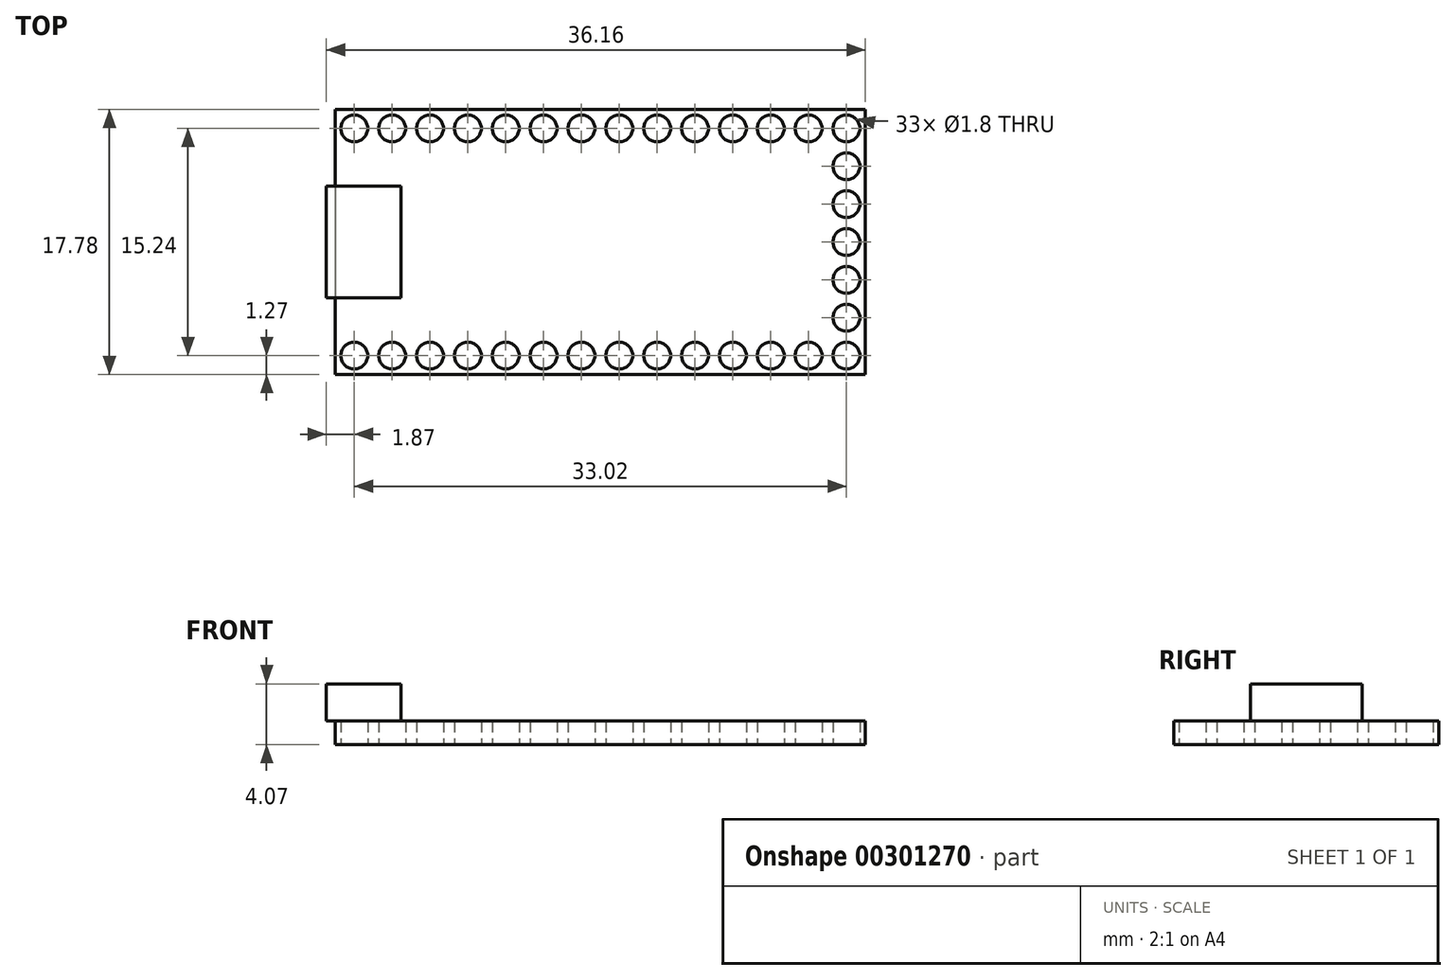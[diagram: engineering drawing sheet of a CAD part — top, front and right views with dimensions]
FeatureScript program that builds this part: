
annotation { "Feature Type Name" : "Feature", "Feature Type Description" : "" }
export const myFeature = defineFeature(function(context is Context, id is Id, definition is map)
    precondition{}
    {
        {
            var Q0;
            Q0=qCreatedBy(makeId("Top.planeOp"),FACE);
            var sketch = newSketch(context, id + "F0", { "sketchPlane" : qUnion([Q0])});
            skLineSegment(sketch, "E0.bottom", {"start": v(0, 8.9) * mm, "end": v(35.56, 8.9) * mm});
            skLineSegment(sketch, "E0.top", {"start": v(0, -8.9) * mm, "end": v(35.56, -8.89) * mm});
            skLineSegment(sketch, "E0.left", {"start": v(0, 8.9) * mm, "end": v(0, -8.9) * mm});
            skLineSegment(sketch, "E0.right", {"start": v(35.56, 8.9) * mm, "end": v(35.56, -8.89) * mm});
            skLineSegment(sketch, "E1.bottom", {"start": v(4.4, 3.75) * mm, "end": v(-0.6, 3.75) * mm});
            skLineSegment(sketch, "E1.top", {"start": v(4.4, -3.75) * mm, "end": v(-0.6, -3.75) * mm});
            skLineSegment(sketch, "E1.left", {"start": v(4.4, 3.75) * mm, "end": v(4.4, -3.75) * mm});
            skLineSegment(sketch, "E1.right", {"start": v(-0.6, 3.75) * mm, "end": v(-0.6, -3.75) * mm});
            skPoint(sketch, "E2", {"position": v(-0.6, 0) * mm});
            skPoint(sketch, "E3", {"position": v(0, 0) * mm});
            skLineSegment(sketch, "E4", {"start": v(1.27, 7.62) * mm, "end": v(35.56, 7.62) * mm, "construction": true});
            skCircle(sketch, "E5", {"center": v(1.27, 7.62) * mm, "radius": 0.9 * mm});
            skCircle(sketch, "E6.1.0.0", {"center": v(3.8, 7.62) * mm, "radius": 0.9 * mm});
            skCircle(sketch, "E6.2.0.0", {"center": v(6.35, 7.62) * mm, "radius": 0.9 * mm});
            skCircle(sketch, "E6.3.0.0", {"center": v(8.89, 7.62) * mm, "radius": 0.9 * mm});
            skCircle(sketch, "E6.4.0.0", {"center": v(11.43, 7.62) * mm, "radius": 0.9 * mm});
            skCircle(sketch, "E6.5.0.0", {"center": v(13.97, 7.62) * mm, "radius": 0.9 * mm});
            skCircle(sketch, "E6.6.0.0", {"center": v(16.5, 7.62) * mm, "radius": 0.9 * mm});
            skCircle(sketch, "E6.7.0.0", {"center": v(19.05, 7.62) * mm, "radius": 0.9 * mm});
            skCircle(sketch, "E6.8.0.0", {"center": v(21.59, 7.62) * mm, "radius": 0.9 * mm});
            skCircle(sketch, "E6.9.0.0", {"center": v(24.13, 7.62) * mm, "radius": 0.9 * mm});
            skCircle(sketch, "E6.10.0.0", {"center": v(26.67, 7.62) * mm, "radius": 0.9 * mm});
            skCircle(sketch, "E6.11.0.0", {"center": v(29.21, 7.62) * mm, "radius": 0.9 * mm});
            skCircle(sketch, "E6.12.0.0", {"center": v(31.75, 7.62) * mm, "radius": 0.9 * mm});
            skCircle(sketch, "E6.13.0.0", {"center": v(34.29, 7.62) * mm, "radius": 0.9 * mm});
            skLineSegment(sketch, "E6.direction1", {"start": v(1.27, 7.62) * mm, "end": v(3.8, 7.62) * mm, "construction": true});
            skLineSegment(sketch, "E7", {"start": v(0, 0) * mm, "end": v(35.56, 0) * mm, "construction": true});
            skCircle(sketch, "E8.MirrorC", {"center": v(6.35, -7.62) * mm, "radius": 0.9 * mm});
            skCircle(sketch, "E9.MirrorC", {"center": v(24.13, -7.62) * mm, "radius": 0.9 * mm});
            skCircle(sketch, "E10.MirrorC", {"center": v(29.21, -7.62) * mm, "radius": 0.9 * mm});
            skCircle(sketch, "E11.MirrorC", {"center": v(19.05, -7.62) * mm, "radius": 0.9 * mm});
            skCircle(sketch, "E12.MirrorC", {"center": v(8.89, -7.62) * mm, "radius": 0.9 * mm});
            skCircle(sketch, "E13.MirrorC", {"center": v(21.59, -7.62) * mm, "radius": 0.9 * mm});
            skCircle(sketch, "E14.MirrorC", {"center": v(11.43, -7.62) * mm, "radius": 0.9 * mm});
            skCircle(sketch, "E15.MirrorC", {"center": v(3.8, -7.62) * mm, "radius": 0.9 * mm});
            skCircle(sketch, "E16.MirrorC", {"center": v(34.29, -7.62) * mm, "radius": 0.9 * mm});
            skCircle(sketch, "E17.MirrorC", {"center": v(31.75, -7.62) * mm, "radius": 0.9 * mm});
            skCircle(sketch, "E18.MirrorC", {"center": v(13.97, -7.62) * mm, "radius": 0.9 * mm});
            skCircle(sketch, "E19.MirrorC", {"center": v(16.51, -7.62) * mm, "radius": 0.9 * mm});
            skCircle(sketch, "E20.MirrorC", {"center": v(26.67, -7.62) * mm, "radius": 0.9 * mm});
            skCircle(sketch, "E21.MirrorC", {"center": v(1.27, -7.62) * mm, "radius": 0.9 * mm});
            skLineSegment(sketch, "E22.MirrorCS", {"start": v(1.27, -7.62) * mm, "end": v(35.56, -7.62) * mm, "construction": true});
            skLineSegment(sketch, "E23.MirrorCS", {"start": v(1.27, -7.62) * mm, "end": v(3.81, -7.62) * mm, "construction": true});
            skCircle(sketch, "E24.1.0.0", {"center": v(34.3, 5.08) * mm, "radius": 0.9 * mm});
            skCircle(sketch, "E24.2.0.0", {"center": v(34.29, 2.54) * mm, "radius": 0.9 * mm});
            skCircle(sketch, "E24.3.0.0", {"center": v(34.29, 0) * mm, "radius": 0.9 * mm});
            skCircle(sketch, "E24.4.0.0", {"center": v(34.29, -2.54) * mm, "radius": 0.9 * mm});
            skCircle(sketch, "E24.5.0.0", {"center": v(34.29, -5.08) * mm, "radius": 0.9 * mm});
            skLineSegment(sketch, "E24.direction1", {"start": v(34.29, 7.62) * mm, "end": v(34.29, 5.08) * mm, "construction": true});
            skSolve(sketch);
        }
        {
            var Q0;
            {var subQ5=sQuery(id+"F0.wireOp",EDGE,"E1.left");Q0=makeQuery(id+"F0.imprint","IMPRINT",FACE,{"disambiguationData":[TD([[makeQuery(id+"F0.imprint","IMPRINT",EDGE,{"derivedFrom":subQ5}),-1.0]])]});}
            var Q1;
            {var subQ5=sQuery(id+"F0.wireOp",EDGE,"E1.right");Q1=makeQuery(id+"F0.imprint","IMPRINT",FACE,{"disambiguationData":[TD([[makeQuery(id+"F0.imprint","IMPRINT",EDGE,{"derivedFrom":subQ5}),1.0]])]});}
            extrude(context, id + "F1", {"entities" : qUnion([Q0, Q1]), "depth" : (2.5 + 1.57) * mm});
        }
        {
            var Q0;
            {var subQ5=sQuery(id+"F0.wireOp",EDGE,"E1.left");Q0=makeQuery(id+"F0.imprint","IMPRINT",FACE,{"disambiguationData":[TD([[makeQuery(id+"F0.imprint","IMPRINT",EDGE,{"derivedFrom":subQ5}),-1.0]])]});}
            var Q1;
            {var subQ5=sQuery(id+"F0.wireOp",EDGE,"E1.right");Q1=makeQuery(id+"F0.imprint","IMPRINT",FACE,{"disambiguationData":[TD([[makeQuery(id+"F0.imprint","IMPRINT",EDGE,{"derivedFrom":subQ5}),1.0]])]});}
            extrude(context, id + "F2", {"entities" : qUnion([Q0, Q1]), "operationType" : NewBodyOperationType.REMOVE, "depth" : 1.57 * mm});
        }
        {
            var Q0;
            {var subQ5=sQuery(id+"F0.wireOp",EDGE,"E1.left");Q0=makeQuery(id+"F0.imprint","IMPRINT",FACE,{"disambiguationData":[TD([[makeQuery(id+"F0.imprint","IMPRINT",EDGE,{"derivedFrom":subQ5}),-1.0]])]});}
            var Q1;
            {var subQ4=sQuery(id+"F0.wireOp",EDGE,"E0.bottom");Q1=makeQuery(id+"F0.imprint","IMPRINT",FACE,{"disambiguationData":[TD([[makeQuery(id+"F0.imprint","IMPRINT",EDGE,{"derivedFrom":subQ4}),-1.0]])]});}
            extrude(context, id + "F3", {"entities" : qUnion([Q0, Q1]), "depth" : 1.57 * mm});
        }
    });
